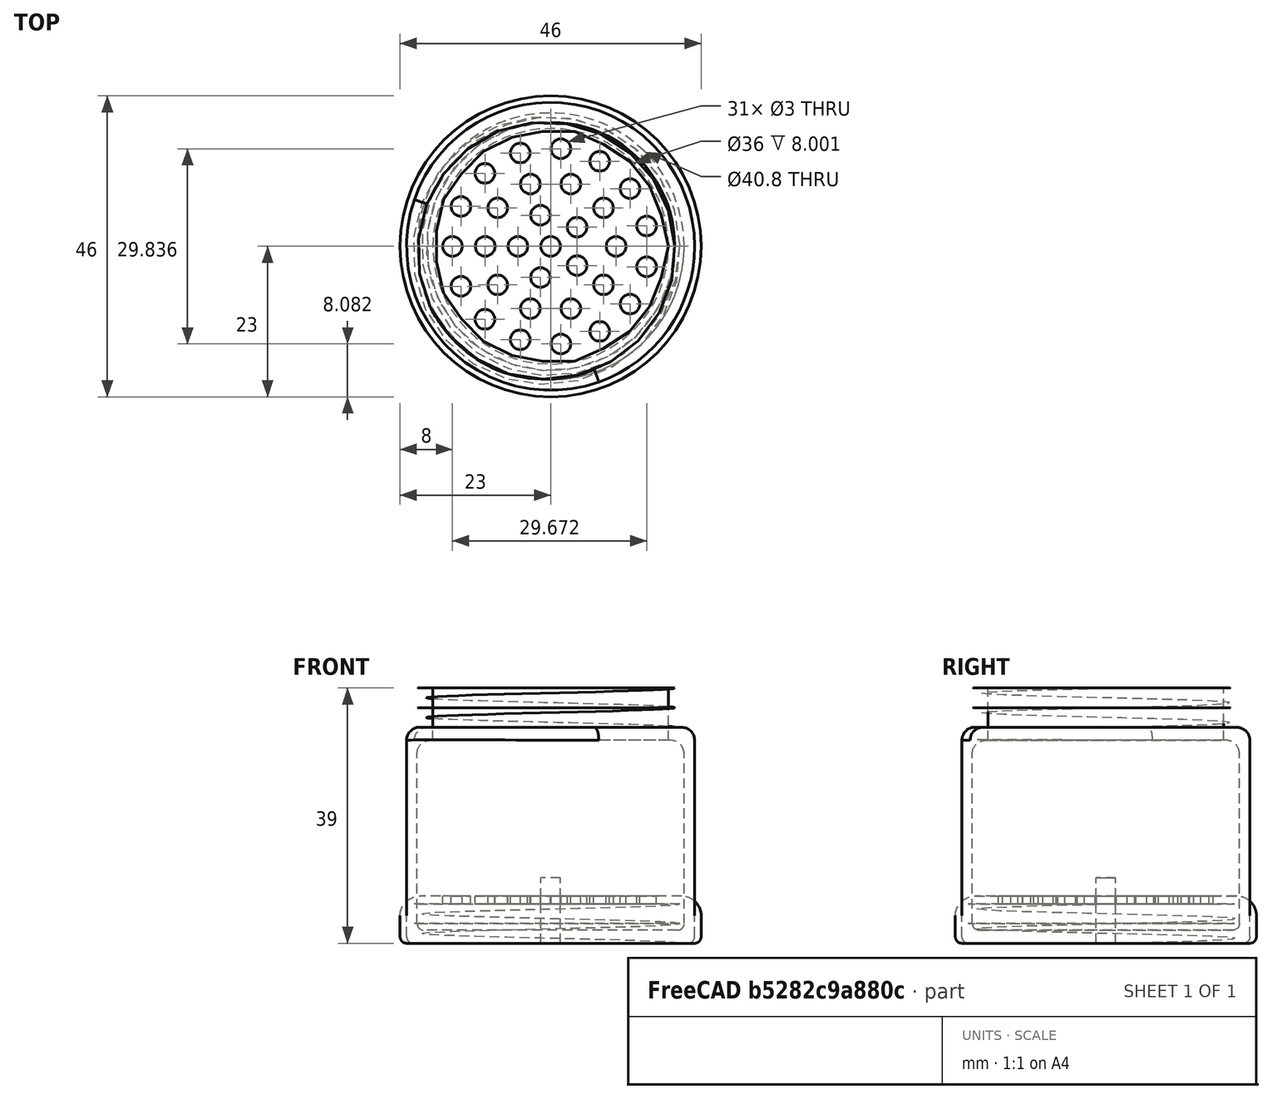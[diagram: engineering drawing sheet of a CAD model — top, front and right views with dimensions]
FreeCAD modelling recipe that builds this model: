
FCSTD DOCUMENT  (FreeCAD 0.19R20514 (Git))
Label: salero
License: All rights reserved
LicenseURL: http://en.wikipedia.org/wiki/All_rights_reserved
objects: Part::Cylinder×5, Part::Cut×4, Part::Part2DObjectPython×2, Part::Helix×2, Part::Sweep×2, Part::Fillet×2, App::Part×2, Part::MultiFuse×1, Part::FeaturePython×1
note: 18 computed .brp shape members not serialized (recipe doc carries the construction recipe); baked Part::Feature solids carry a one-line shape summary decoded from their .brp

FEATURE [Part::Part2DObjectPython] VThreadProfile  # Draft 2D object (typed FeaturePython)
  Area = 1214.33
  Closed = true
  Continuity = C2
  Instructions = Expand this with the ... button to view instructions | Sweep this object along a helix of the same pitch to produce your thread. | It is recommended to make the helix in the ThreadProfile workbench. | If there is an active Body the ThreadProfile object will be put into it.,If not it can be dragged and dropped into the body later. | If there is an active Body when the helix is made there will be made a ShapeBinder for it | For internal threads you will need to cut the Sweep object out of a cylinder, or if using Part Design sweep it as a Subtractive Pipe. | Always use Frenet mode | I have provided some presets, but it is possible there could be some errors.  Double check for mission critical applications. | Also, the tolerances might be different from what you wish to have.  I believe the internal minor diameters are all minimum and the external are all maximum.
  InternalOrExternal = 1
  MakeFace = true
  MinorDiameter = 37.955
  Parameterization = 1
  Pitch = 3
  Points = (719) [(18.9697,0.165776,0),(18.9608,0.331422,0),(18.9507,0.496931,0),(18.9393,0.662297,0),(18.9268,0.827512,0),(18.913,0.992571,0),(18.898,1.15746,0),+712 more]
  Presets = 0
  Quality = 1
  ThreadCount = 2
  Version = 1.51
  external_data = [-0.00235387,-0.00461052,-0.00677828,-0.00886428,-0.0108747,-0.0128149,-0.0146895,-0.0165028,-0.0182584,-0.0199597,-0.0216095,-0.0232106,-0.0247653,-0.0262759,-0.0277444,-0.0291725,-0.0305621,-0.0319145,-0.0332313,-0.0345138,-0.0357632,+698 more]
  internal_data = [0,0,0,0,0,0,0,0,0,0,0,0,0,0,0,0,0,0,0,0,0,0,0,0,0,0,0,0,0,0,0,0,0,0,0,0,0,0,0,0,0,0,0,0,0,0,0,0,0,0,0,0,0,0,0,0,0,0,0,0,0,0,0,0,0,0,0,0,0,0,0,0,0,0,0,0,0,0,0,0,0,0,0,0,0,0,0,0,0,0,0,0,0,0,0,0,0,0,0,0,0,0,0,0,0,0,0,0,0,0,0,0,0,0,0,0,0,0,0,0,+599 more]
  preset_names = <blob: 3959 chars omitted>
  presets_data = [0,0,0,2.20878,24.1173,24.6888,0.25,0.693,0.729,0.25,0.793,0.829,0.25,0.893,0.929,0.3,1.032,1.075,0.35,1.171,1.221,0.35,1.371,1.421,0.4,1.509,1.567,0.45,1.648,1.713,0.45,1.948,2.013,0.5,2.387,2.459,0.6,2.764,2.85,0.7,3.141,3.242,0.75,3.58,+712 more]
FEATURE [Part::Helix] Helix
  Angle = 0
  AttacherType = Attacher::AttachEngine3D
  Height = 6
  LocalCoord = 0
  Pitch = 3
  Radius = 1
  Style = 0
  expr: .Placement.Rotation.Axis.z = VThreadProfile.Placement.Rotation.Axis.z
  expr: .Placement.Rotation.Axis.y = VThreadProfile.Placement.Rotation.Axis.y
  expr: .Placement.Rotation.Axis.x = VThreadProfile.Placement.Rotation.Axis.x
  expr: .Placement.Rotation.Angle = VThreadProfile.Placement.Rotation.Angle
  expr: .Placement.Base.z = VThreadProfile.Placement.Base.z
  expr: .Placement.Base.y = VThreadProfile.Placement.Base.y
  expr: .Placement.Base.x = VThreadProfile.Placement.Base.x
  expr: Height = VThreadProfile.ThreadCount * VThreadProfile.Pitch
  expr: Pitch = VThreadProfile.Pitch
FEATURE [Part::Sweep] Sweep
  Frenet = true
  Placement = pos=(0,0,33) rot=(0,0,1;0rad)
  Sections = -> [VThreadProfile]
  Solid = true
  Spine = -> Helix [Edge1,Edge2]
  Transition = 1
FEATURE [Part::Cylinder] Cylinder  label="Cilindro"
  Angle = 360
  AttacherType = Attacher::AttachEngine3D
  Height = 15
  Placement = pos=(0,0,29) rot=(0,0,1;0rad)
  Radius = 18
FEATURE [Part::Cylinder] Cylinder001  label="Cilindro001"
  Angle = 360
  AttacherType = Attacher::AttachEngine3D
  Height = 33
  Radius = 22
FEATURE [Part::Cylinder] Cylinder002  label="Cilindro002"
  Angle = 360
  AttacherType = Attacher::AttachEngine3D
  Height = 29
  Placement = pos=(0,0,2) rot=(0,0,1;0rad)
  Radius = 20.4
FEATURE [Part::Cut] Cut001
  Base = -> Cylinder001
  Tool = -> Cylinder002
FEATURE [Part::MultiFuse] Fusion
  Shapes = -> [Sweep,Cut001]
FEATURE [Part::Cut] Cut
  Base = -> Fusion
  Tool = -> Cylinder
FEATURE [Part::Fillet] Fillet
  Base = -> Cut
  Edges = 4 edges: [Edge1 r=2,Edge3 r=1,Edge12 r=2,Edge14 r=1]
FEATURE [App::Part] Part  label="Cuerpo"
  Group = -> [VThreadProfile,Helix,Sweep,Cylinder,Cylinder001,Cylinder002,Cut001,Fusion,Cut,Fillet]
  Origin = -> Origin
  Placement = pos=(0,50,0) rot=(0,0,1;0rad)
FEATURE [Part::Part2DObjectPython] VThreadProfile001  # Draft 2D object (typed FeaturePython)
  Area = 1317.17
  Closed = true
  Continuity = C2
  Instructions = Expand this with the ... button to view instructions | Sweep this object along a helix of the same pitch to produce your thread. | It is recommended to make the helix in the ThreadProfile workbench. | If there is an active Body the ThreadProfile object will be put into it.,If not it can be dragged and dropped into the body later. | If there is an active Body when the helix is made there will be made a ShapeBinder for it | For internal threads you will need to cut the Sweep object out of a cylinder, or if using Part Design sweep it as a Subtractive Pipe. | Always use Frenet mode | I have provided some presets, but it is possible there could be some errors.  Double check for mission critical applications. | Also, the tolerances might be different from what you wish to have.  I believe the internal minor diameters are all minimum and the external are all maximum.
  InternalOrExternal = 0
  MakeFace = true
  MinorDiameter = 39.5
  Parameterization = 1
  Pitch = 3
  Points = (719) [(19.7492,0.172589,0),(19.747,0.345164,0),(19.7432,0.517714,0),(19.7379,0.690223,0),(19.7312,0.86268,0),(19.7229,1.03507,0),(19.7131,1.20738,0),+712 more]
  Presets = 0
  Quality = 1
  ThreadCount = 2
  Version = 1.51
  external_data = [-0.00235387,-0.00461052,-0.00677828,-0.00886428,-0.0108747,-0.0128149,-0.0146895,-0.0165028,-0.0182584,-0.0199597,-0.0216095,-0.0232106,-0.0247653,-0.0262759,-0.0277444,-0.0291725,-0.0305621,-0.0319145,-0.0332313,-0.0345138,-0.0357632,+698 more]
  internal_data = [0,0,0,0,0,0,0,0,0,0,0,0,0,0,0,0,0,0,0,0,0,0,0,0,0,0,0,0,0,0,0,0,0,0,0,0,0,0,0,0,0,0,0,0,0,0,0,0,0,0,0,0,0,0,0,0,0,0,0,0,0,0,0,0,0,0,0,0,0,0,0,0,0,0,0,0,0,0,0,0,0,0,0,0,0,0,0,0,0,0,0,0,0,0,0,0,0,0,0,0,0,0,0,0,0,0,0,0,0,0,0,0,0,0,0,0,0,0,0,0,+599 more]
  preset_names = <blob: 3959 chars omitted>
  presets_data = [0,0,0,2.20878,24.1173,24.6888,0.25,0.693,0.729,0.25,0.793,0.829,0.25,0.893,0.929,0.3,1.032,1.075,0.35,1.171,1.221,0.35,1.371,1.421,0.4,1.509,1.567,0.45,1.648,1.713,0.45,1.948,2.013,0.5,2.387,2.459,0.6,2.764,2.85,0.7,3.141,3.242,0.75,3.58,+712 more]
FEATURE [Part::Helix] Helix001
  Angle = 0
  AttacherType = Attacher::AttachEngine3D
  Height = 6
  LocalCoord = 0
  Pitch = 3
  Radius = 1
  Style = 0
  expr: .Placement.Rotation.Axis.z = VThreadProfile001.Placement.Rotation.Axis.z
  expr: .Placement.Rotation.Axis.y = VThreadProfile001.Placement.Rotation.Axis.y
  expr: .Placement.Rotation.Axis.x = VThreadProfile001.Placement.Rotation.Axis.x
  expr: .Placement.Rotation.Angle = VThreadProfile001.Placement.Rotation.Angle
  expr: .Placement.Base.z = VThreadProfile001.Placement.Base.z
  expr: .Placement.Base.y = VThreadProfile001.Placement.Base.y
  expr: .Placement.Base.x = VThreadProfile001.Placement.Base.x
  expr: Height = VThreadProfile001.ThreadCount * VThreadProfile001.Pitch
  expr: Pitch = VThreadProfile001.Pitch
FEATURE [Part::Sweep] Sweep001
  Frenet = true
  Sections = -> [VThreadProfile001]
  Solid = true
  Spine = -> Helix001 [Edge1,Edge2]
  Transition = 1
FEATURE [Part::Cylinder] Cylinder003  label="Cilindro003"
  Angle = 360
  AttacherType = Attacher::AttachEngine3D
  Height = 7.2
  Radius = 23
FEATURE [Part::Cut] Cut002
  Base = -> Cylinder003
  Tool = -> Sweep001
FEATURE [Part::Cylinder] Cylinder004  label="Cilindro004"
  Angle = 360
  AttacherType = Attacher::AttachEngine3D
  Height = 10
  Radius = 1.5
FEATURE [Part::FeaturePython] Array  # Draft array (typed FeaturePython)
  Angle = 360
  ArrayType = 2
  Axis = (0,0,1)
  Base = -> Cylinder004
  Center = (0,0,0)
  Count = 31
  ExpandArray = false
  Fuse = false
  IntervalAxis = (0,0,0)
  IntervalX = (1,0,0)
  IntervalY = (0,1,0)
  IntervalZ = (0,0,1)
  NumberCircles = 4
  NumberPolar = 1
  NumberX = 1
  NumberY = 1
  NumberZ = 1
  PlacementList = 31 placements: [(0,0,0),(-5,0,0),(-1.54508,-4.75528,0),(4.04508,-2.93893,0),(4.04508,2.93893,0),(-1.54508,4.75528,0),(-10,0,0),(-8.09017,-5.87785,0),(-3.09017,-9.51057,0),(3.09017,-9.51057,0),(8.09017,-5.87785,0),(10,-1.22465e-15,0),(8.09017,5.87785,0),(3.09017,9.51057,0),(-3.09017,9.51057,0),(-8.09017,5.87785,0),(-15,0,0),(-13.7032,-6.10105,0),(-10.037,-11.1472,0),(-4.63525,-14.2658,0),(1.56793,-14.9178,0),+10 more]
  RadialDistance = 5
  ScaleList = (31) [(1,1,1),(1,1,1),(1,1,1),(1,1,1),(1,1,1),(1,1,1),(1,1,1),(1,1,1),(1,1,1),(1,1,1),(1,1,1),(1,1,1),(1,1,1),(1,1,1),(1,1,1),(1,1,1),(1,1,1),(1,1,1),+13 more]
  Symmetry = 1
  TangentialDistance = 6
FEATURE [Part::Cut] Cut003
  Base = -> Cut002
  Tool = -> Array
FEATURE [Part::Fillet] Fillet001
  Base = -> Cut003
  Edges = 2 edges: [Edge1 r=3,Edge3 r=1]
FEATURE [App::Part] Part001  label="Tapa"
  Group = -> [VThreadProfile001,Helix001,Sweep001,Cylinder003,Cut002,Cylinder004,Array,Cut003,Fillet001]
  Origin = -> Origin001
